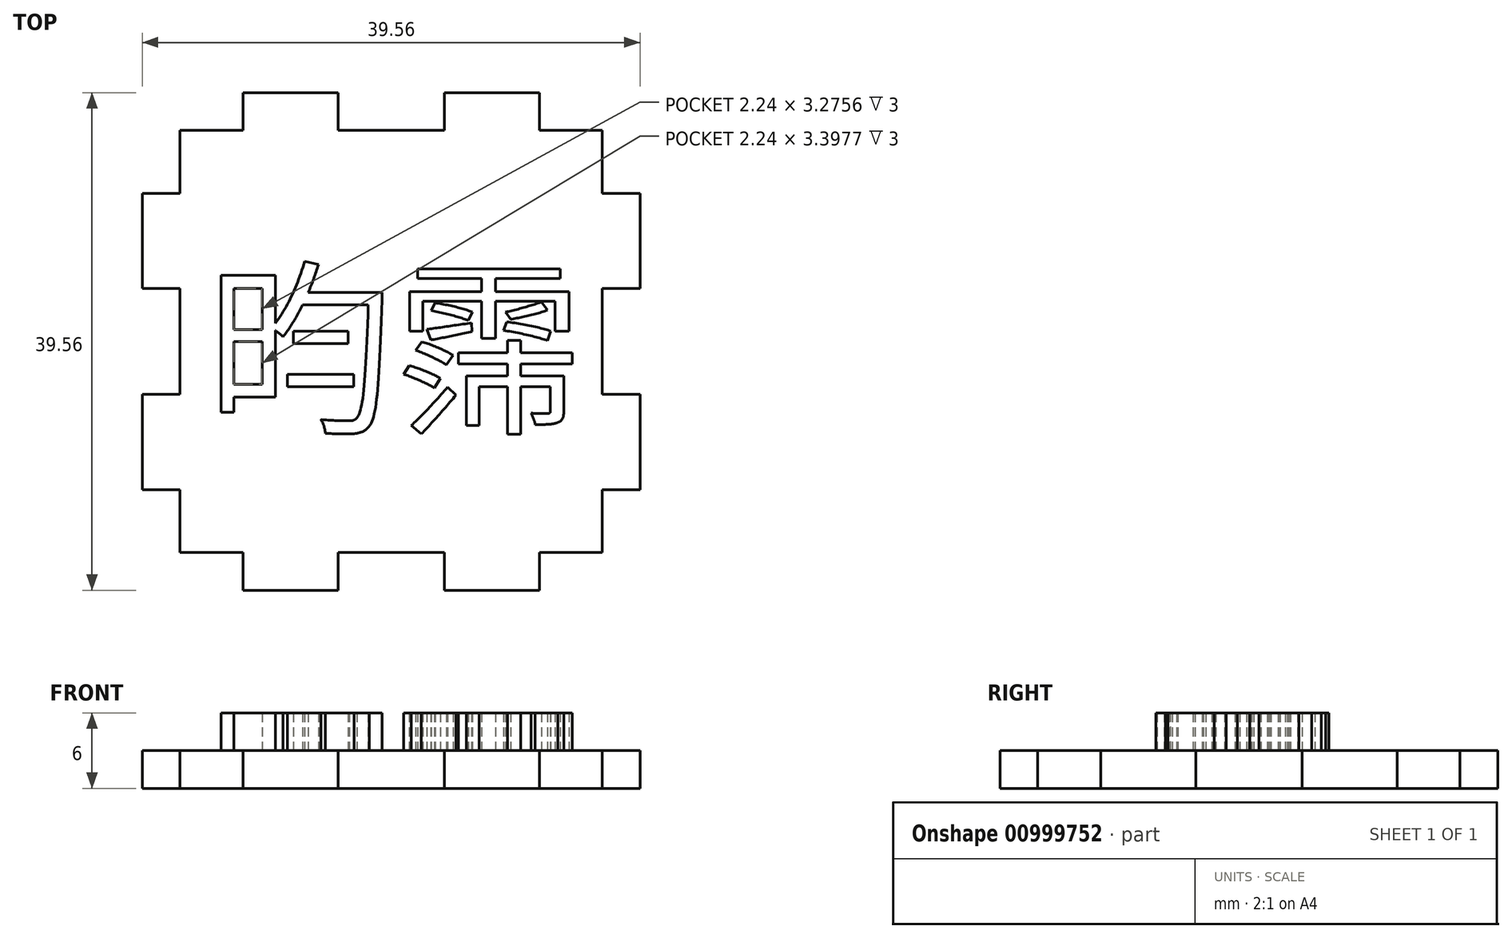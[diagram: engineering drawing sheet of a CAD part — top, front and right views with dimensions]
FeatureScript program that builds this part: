
annotation { "Feature Type Name" : "Feature", "Feature Type Description" : "" }
export const myFeature = defineFeature(function(context is Context, id is Id, definition is map)
    precondition{}
    {
        {
            var Q0;
            Q0=qCreatedBy(makeId("Top.planeOp"),FACE);
            var sketch = newSketch(context, id + "F0", { "sketchPlane" : qUnion([Q0])});
            skLineSegment(sketch, "E0.bottom", {"start": v(17, -17) * mm, "end": v(-17, -17) * mm});
            skLineSegment(sketch, "E0.top", {"start": v(17, 17) * mm, "end": v(-17, 17) * mm});
            skLineSegment(sketch, "E0.left", {"start": v(17, -17) * mm, "end": v(17, 17) * mm});
            skLineSegment(sketch, "E0.right", {"start": v(-17, -17) * mm, "end": v(-17, 17) * mm});
            skPoint(sketch, "E0.middle", {"position": v(0, 0) * mm});
            skSolve(sketch);
        }
        {
            var Q0;
            Q0 = qSketchRegion(id + "F0", true);
            extrude(context, id + "F1", {"entities" : qUnion([Q0]), "depth" : 3 * mm, "offsetDistance" : 25 * mm});
        }
        {
            var Q0;
            Q0=makeQuery(id+"F1.opExtrude","CAP_FACE",FACE,{"disambiguationData":[OSD([sQuery(id+"F0.wireOp",EDGE,"E0.bottom"),sQuery(id+"F0.wireOp",EDGE,"E0.top"),sQuery(id+"F0.wireOp",EDGE,"E0.left"),sQuery(id+"F0.wireOp",EDGE,"E0.right")])],"isStart":false});
            var sketch = newSketch(context, id + "F2", { "sketchPlane" : qUnion([Q0])});
            skLineSegment(sketch, "E1.bottom", {"start": v(-17, 12) * mm, "end": v(-20, 12) * mm});
            skLineSegment(sketch, "E1.top", {"start": v(-17, 4) * mm, "end": v(-20, 4) * mm});
            skLineSegment(sketch, "E1.left", {"start": v(-17, 12) * mm, "end": v(-17, 4) * mm});
            skLineSegment(sketch, "E1.right", {"start": v(-20, 12) * mm, "end": v(-20, 4) * mm});
            skLineSegment(sketch, "E2.MirrorCS", {"start": v(-17, -12) * mm, "end": v(-20, -12) * mm});
            skLineSegment(sketch, "E3.MirrorCS", {"start": v(-17, -12) * mm, "end": v(-17, -4) * mm});
            skLineSegment(sketch, "E4.MirrorCS", {"start": v(-20, -12) * mm, "end": v(-20, -4) * mm});
            skLineSegment(sketch, "E5.MirrorCS", {"start": v(-17, -4) * mm, "end": v(-20, -4) * mm});
            skLineSegment(sketch, "E6.1.0", {"start": v(-4, -17) * mm, "end": v(-4, -20) * mm});
            skLineSegment(sketch, "E6.1.1", {"start": v(4, -17) * mm, "end": v(4, -20) * mm});
            skLineSegment(sketch, "E6.1.2", {"start": v(12, -17) * mm, "end": v(4, -17) * mm});
            skLineSegment(sketch, "E6.1.3", {"start": v(-12, -17) * mm, "end": v(-12, -20) * mm});
            skLineSegment(sketch, "E6.1.4", {"start": v(12, -17) * mm, "end": v(12, -20) * mm});
            skLineSegment(sketch, "E6.1.5", {"start": v(-12, -17) * mm, "end": v(-4, -17) * mm});
            skLineSegment(sketch, "E6.1.6", {"start": v(12, -20) * mm, "end": v(4, -20) * mm});
            skLineSegment(sketch, "E6.1.7", {"start": v(-12, -20) * mm, "end": v(-4, -20) * mm});
            skLineSegment(sketch, "E6.2.0", {"start": v(17, -4) * mm, "end": v(20, -4) * mm});
            skLineSegment(sketch, "E6.2.1", {"start": v(17, 4) * mm, "end": v(20, 4) * mm});
            skLineSegment(sketch, "E6.2.2", {"start": v(17, 12) * mm, "end": v(17, 4) * mm});
            skLineSegment(sketch, "E6.2.3", {"start": v(17, -12) * mm, "end": v(20, -12) * mm});
            skLineSegment(sketch, "E6.2.4", {"start": v(17, 12) * mm, "end": v(20, 12) * mm});
            skLineSegment(sketch, "E6.2.5", {"start": v(17, -12) * mm, "end": v(17, -4) * mm});
            skLineSegment(sketch, "E6.2.6", {"start": v(20, 12) * mm, "end": v(20, 4) * mm});
            skLineSegment(sketch, "E6.2.7", {"start": v(20, -12) * mm, "end": v(20, -4) * mm});
            skLineSegment(sketch, "E6.3.0", {"start": v(4, 17) * mm, "end": v(4, 20) * mm});
            skLineSegment(sketch, "E6.3.1", {"start": v(-4, 17) * mm, "end": v(-4, 20) * mm});
            skLineSegment(sketch, "E6.3.2", {"start": v(-12, 17) * mm, "end": v(-4, 17) * mm});
            skLineSegment(sketch, "E6.3.3", {"start": v(12, 17) * mm, "end": v(12, 20) * mm});
            skLineSegment(sketch, "E6.3.4", {"start": v(-12, 17) * mm, "end": v(-12, 20) * mm});
            skLineSegment(sketch, "E6.3.5", {"start": v(12, 17) * mm, "end": v(4, 17) * mm});
            skLineSegment(sketch, "E6.3.6", {"start": v(-12, 20) * mm, "end": v(-4, 20) * mm});
            skLineSegment(sketch, "E6.3.7", {"start": v(12, 20) * mm, "end": v(4, 20) * mm});
            skPoint(sketch, "E6.center", {"position": v(0, 0) * mm});
            skSolve(sketch);
        }
        {
            var Q0;
            Q0 = qSketchRegion(id + "F2", true);
            extrude(context, id + "F3", {"entities" : qUnion([Q0]), "operationType" : NewBodyOperationType.ADD, "oppositeDirection" : true, "depth" : 3 * mm, "offsetDistance" : 25 * mm});
        }
        {
            var Q0;
            Q0=makeQuery(id+"F3.boolean.opBoolean","MERGE",FACE,{"derivedFrom":[makeQuery(id+"F1.opExtrude","CAP_FACE",FACE,{"disambiguationData":[OSD([sQuery(id+"F0.wireOp",EDGE,"E0.bottom"),sQuery(id+"F0.wireOp",EDGE,"E0.top"),sQuery(id+"F0.wireOp",EDGE,"E0.left"),sQuery(id+"F0.wireOp",EDGE,"E0.right")])],"isStart":false}),makeQuery(id+"F3.opExtrude","CAP_FACE",FACE,{"disambiguationData":[OSD([sQuery(id+"F2.wireOp",EDGE,"E1.bottom"),sQuery(id+"F2.wireOp",EDGE,"E1.top"),sQuery(id+"F2.wireOp",EDGE,"E1.left"),sQuery(id+"F2.wireOp",EDGE,"E1.right")])],"isStart":true}),makeQuery(id+"F3.opExtrude","CAP_FACE",FACE,{"disambiguationData":[OSD([sQuery(id+"F2.wireOp",EDGE,"E2.MirrorCS"),sQuery(id+"F2.wireOp",EDGE,"E3.MirrorCS"),sQuery(id+"F2.wireOp",EDGE,"E4.MirrorCS"),sQuery(id+"F2.wireOp",EDGE,"E5.MirrorCS")])],"isStart":true}),makeQuery(id+"F3.opExtrude","CAP_FACE",FACE,{"disambiguationData":[OSD([sQuery(id+"F2.wireOp",EDGE,"E6.1.0"),sQuery(id+"F2.wireOp",EDGE,"E6.1.3"),sQuery(id+"F2.wireOp",EDGE,"E6.1.5"),sQuery(id+"F2.wireOp",EDGE,"E6.1.7")])],"isStart":true}),makeQuery(id+"F3.opExtrude","CAP_FACE",FACE,{"disambiguationData":[OSD([sQuery(id+"F2.wireOp",EDGE,"E6.1.1"),sQuery(id+"F2.wireOp",EDGE,"E6.1.2"),sQuery(id+"F2.wireOp",EDGE,"E6.1.4"),sQuery(id+"F2.wireOp",EDGE,"E6.1.6")])],"isStart":true}),makeQuery(id+"F3.opExtrude","CAP_FACE",FACE,{"disambiguationData":[OSD([sQuery(id+"F2.wireOp",EDGE,"E6.2.0"),sQuery(id+"F2.wireOp",EDGE,"E6.2.3"),sQuery(id+"F2.wireOp",EDGE,"E6.2.5"),sQuery(id+"F2.wireOp",EDGE,"E6.2.7")])],"isStart":true}),makeQuery(id+"F3.opExtrude","CAP_FACE",FACE,{"disambiguationData":[OSD([sQuery(id+"F2.wireOp",EDGE,"E6.2.1"),sQuery(id+"F2.wireOp",EDGE,"E6.2.2"),sQuery(id+"F2.wireOp",EDGE,"E6.2.4"),sQuery(id+"F2.wireOp",EDGE,"E6.2.6")])],"isStart":true}),makeQuery(id+"F3.opExtrude","CAP_FACE",FACE,{"disambiguationData":[OSD([sQuery(id+"F2.wireOp",EDGE,"E6.3.0"),sQuery(id+"F2.wireOp",EDGE,"E6.3.3"),sQuery(id+"F2.wireOp",EDGE,"E6.3.5"),sQuery(id+"F2.wireOp",EDGE,"E6.3.7")])],"isStart":true}),makeQuery(id+"F3.opExtrude","CAP_FACE",FACE,{"disambiguationData":[OSD([sQuery(id+"F2.wireOp",EDGE,"E6.3.1"),sQuery(id+"F2.wireOp",EDGE,"E6.3.2"),sQuery(id+"F2.wireOp",EDGE,"E6.3.4"),sQuery(id+"F2.wireOp",EDGE,"E6.3.6")])],"isStart":true})]});
            var sketch = newSketch(context, id + "F4", { "sketchPlane" : qUnion([Q0])});
            skLineSegment(sketch, "E7.0", {"start": v(11.78, -16.78) * mm, "end": v(16.78, -16.78) * mm});
            skLineSegment(sketch, "E7.1", {"start": v(11.78, -19.78) * mm, "end": v(11.78, -16.78) * mm});
            skLineSegment(sketch, "E7.2", {"start": v(4.22, -19.78) * mm, "end": v(11.78, -19.78) * mm});
            skLineSegment(sketch, "E7.3", {"start": v(4.22, -16.78) * mm, "end": v(4.22, -19.78) * mm});
            skLineSegment(sketch, "E7.4", {"start": v(-4.22, -16.78) * mm, "end": v(4.22, -16.78) * mm});
            skLineSegment(sketch, "E7.5", {"start": v(-4.22, -19.78) * mm, "end": v(-4.22, -16.78) * mm});
            skLineSegment(sketch, "E7.6", {"start": v(-11.78, -19.78) * mm, "end": v(-4.22, -19.78) * mm});
            skLineSegment(sketch, "E7.7", {"start": v(-11.78, -16.78) * mm, "end": v(-11.78, -19.78) * mm});
            skLineSegment(sketch, "E7.8", {"start": v(-16.78, -16.78) * mm, "end": v(-11.78, -16.78) * mm});
            skLineSegment(sketch, "E7.9", {"start": v(-16.78, -11.78) * mm, "end": v(-16.78, -16.78) * mm});
            skLineSegment(sketch, "E7.10", {"start": v(-19.78, -11.78) * mm, "end": v(-16.78, -11.78) * mm});
            skLineSegment(sketch, "E7.11", {"start": v(16.78, -16.78) * mm, "end": v(16.78, -11.78) * mm});
            skLineSegment(sketch, "E7.12", {"start": v(-19.78, -4.22) * mm, "end": v(-19.78, -11.78) * mm});
            skLineSegment(sketch, "E7.13", {"start": v(-16.78, -4.22) * mm, "end": v(-19.78, -4.22) * mm});
            skLineSegment(sketch, "E7.14", {"start": v(11.78, 16.78) * mm, "end": v(11.78, 19.78) * mm});
            skLineSegment(sketch, "E7.15", {"start": v(16.78, 16.78) * mm, "end": v(11.78, 16.78) * mm});
            skLineSegment(sketch, "E7.16", {"start": v(16.78, 11.78) * mm, "end": v(16.78, 16.78) * mm});
            skLineSegment(sketch, "E7.17", {"start": v(19.78, 11.78) * mm, "end": v(16.78, 11.78) * mm});
            skLineSegment(sketch, "E7.18", {"start": v(19.78, 4.22) * mm, "end": v(19.78, 11.78) * mm});
            skLineSegment(sketch, "E7.19", {"start": v(16.78, 4.22) * mm, "end": v(19.78, 4.22) * mm});
            skLineSegment(sketch, "E7.20", {"start": v(16.78, -11.78) * mm, "end": v(19.78, -11.78) * mm});
            skLineSegment(sketch, "E7.21", {"start": v(19.78, -11.78) * mm, "end": v(19.78, -4.22) * mm});
            skLineSegment(sketch, "E7.22", {"start": v(19.78, -4.22) * mm, "end": v(16.78, -4.22) * mm});
            skLineSegment(sketch, "E7.23", {"start": v(16.78, -4.22) * mm, "end": v(16.78, 4.22) * mm});
            skLineSegment(sketch, "E7.24", {"start": v(11.78, 19.78) * mm, "end": v(4.22, 19.78) * mm});
            skLineSegment(sketch, "E7.25", {"start": v(4.22, 19.78) * mm, "end": v(4.22, 16.78) * mm});
            skLineSegment(sketch, "E7.26", {"start": v(4.22, 16.78) * mm, "end": v(-4.22, 16.78) * mm});
            skLineSegment(sketch, "E7.27", {"start": v(-4.22, 16.78) * mm, "end": v(-4.22, 19.78) * mm});
            skLineSegment(sketch, "E7.28", {"start": v(-4.22, 19.78) * mm, "end": v(-11.78, 19.78) * mm});
            skLineSegment(sketch, "E7.29", {"start": v(-11.78, 19.78) * mm, "end": v(-11.78, 16.78) * mm});
            skLineSegment(sketch, "E7.30", {"start": v(-11.78, 16.78) * mm, "end": v(-16.78, 16.78) * mm});
            skLineSegment(sketch, "E7.31", {"start": v(-16.78, 16.78) * mm, "end": v(-16.78, 11.78) * mm});
            skLineSegment(sketch, "E7.32", {"start": v(-16.78, 11.78) * mm, "end": v(-19.78, 11.78) * mm});
            skLineSegment(sketch, "E7.33", {"start": v(-19.78, 11.78) * mm, "end": v(-19.78, 4.22) * mm});
            skLineSegment(sketch, "E7.34", {"start": v(-19.78, 4.22) * mm, "end": v(-16.78, 4.22) * mm});
            skLineSegment(sketch, "E7.35", {"start": v(-16.78, 4.22) * mm, "end": v(-16.78, -4.22) * mm});
            skLineSegment(sketch, "E8.bottom", {"start": v(25.94, -26.08) * mm, "end": v(-25.94, -26.08) * mm});
            skLineSegment(sketch, "E8.top", {"start": v(25.94, 26.08) * mm, "end": v(-25.94, 26.08) * mm});
            skLineSegment(sketch, "E8.left", {"start": v(25.94, -26.08) * mm, "end": v(25.94, 26.08) * mm});
            skLineSegment(sketch, "E8.right", {"start": v(-25.94, -26.08) * mm, "end": v(-25.94, 26.08) * mm});
            skPoint(sketch, "E8.middle", {"position": v(0, 0) * mm});
            skSolve(sketch);
        }
        {
            var Q0;
            Q0 = qSketchRegion(id + "F4", true);
            extrude(context, id + "F5", {"entities" : qUnion([Q0]), "operationType" : NewBodyOperationType.REMOVE, "endBound" : BoundingType.THROUGH_ALL, "oppositeDirection" : true, "depth" : 25 * mm, "offsetDistance" : 25 * mm});
        }
        {
            var Q0;
            Q0=makeQuery(id+"F3.boolean.opBoolean","MERGE",FACE,{"derivedFrom":[makeQuery(id+"F1.opExtrude","CAP_FACE",FACE,{"disambiguationData":[OSD([sQuery(id+"F0.wireOp",EDGE,"E0.bottom"),sQuery(id+"F0.wireOp",EDGE,"E0.top"),sQuery(id+"F0.wireOp",EDGE,"E0.left"),sQuery(id+"F0.wireOp",EDGE,"E0.right")])],"isStart":false}),makeQuery(id+"F3.opExtrude","CAP_FACE",FACE,{"disambiguationData":[OSD([sQuery(id+"F2.wireOp",EDGE,"E1.bottom"),sQuery(id+"F2.wireOp",EDGE,"E1.top"),sQuery(id+"F2.wireOp",EDGE,"E1.left"),sQuery(id+"F2.wireOp",EDGE,"E1.right")])],"isStart":true}),makeQuery(id+"F3.opExtrude","CAP_FACE",FACE,{"disambiguationData":[OSD([sQuery(id+"F2.wireOp",EDGE,"E2.MirrorCS"),sQuery(id+"F2.wireOp",EDGE,"E3.MirrorCS"),sQuery(id+"F2.wireOp",EDGE,"E4.MirrorCS"),sQuery(id+"F2.wireOp",EDGE,"E5.MirrorCS")])],"isStart":true}),makeQuery(id+"F3.opExtrude","CAP_FACE",FACE,{"disambiguationData":[OSD([sQuery(id+"F2.wireOp",EDGE,"E6.1.0"),sQuery(id+"F2.wireOp",EDGE,"E6.1.3"),sQuery(id+"F2.wireOp",EDGE,"E6.1.5"),sQuery(id+"F2.wireOp",EDGE,"E6.1.7")])],"isStart":true}),makeQuery(id+"F3.opExtrude","CAP_FACE",FACE,{"disambiguationData":[OSD([sQuery(id+"F2.wireOp",EDGE,"E6.1.1"),sQuery(id+"F2.wireOp",EDGE,"E6.1.2"),sQuery(id+"F2.wireOp",EDGE,"E6.1.4"),sQuery(id+"F2.wireOp",EDGE,"E6.1.6")])],"isStart":true}),makeQuery(id+"F3.opExtrude","CAP_FACE",FACE,{"disambiguationData":[OSD([sQuery(id+"F2.wireOp",EDGE,"E6.2.0"),sQuery(id+"F2.wireOp",EDGE,"E6.2.3"),sQuery(id+"F2.wireOp",EDGE,"E6.2.5"),sQuery(id+"F2.wireOp",EDGE,"E6.2.7")])],"isStart":true}),makeQuery(id+"F3.opExtrude","CAP_FACE",FACE,{"disambiguationData":[OSD([sQuery(id+"F2.wireOp",EDGE,"E6.2.1"),sQuery(id+"F2.wireOp",EDGE,"E6.2.2"),sQuery(id+"F2.wireOp",EDGE,"E6.2.4"),sQuery(id+"F2.wireOp",EDGE,"E6.2.6")])],"isStart":true}),makeQuery(id+"F3.opExtrude","CAP_FACE",FACE,{"disambiguationData":[OSD([sQuery(id+"F2.wireOp",EDGE,"E6.3.0"),sQuery(id+"F2.wireOp",EDGE,"E6.3.3"),sQuery(id+"F2.wireOp",EDGE,"E6.3.5"),sQuery(id+"F2.wireOp",EDGE,"E6.3.7")])],"isStart":true}),makeQuery(id+"F3.opExtrude","CAP_FACE",FACE,{"disambiguationData":[OSD([sQuery(id+"F2.wireOp",EDGE,"E6.3.1"),sQuery(id+"F2.wireOp",EDGE,"E6.3.2"),sQuery(id+"F2.wireOp",EDGE,"E6.3.4"),sQuery(id+"F2.wireOp",EDGE,"E6.3.6")])],"isStart":true})]});
            var sketch = newSketch(context, id + "F6", { "sketchPlane" : qUnion([Q0])});
            skText(sketch, "E9", { "text": "昀霈", "fontName": "NotoSansCJKtc-Regular.otf"});
            const initialGuessF6  = {"E9": [-0.01476, -0.00622, 1, 0, 0.01082]};
            skSetInitialGuess(sketch, initialGuessF6);
            skSolve(sketch);
        }
        {
            var Q0;
            Q0 = qSketchRegion(id + "F6", true);
            extrude(context, id + "F7", {"entities" : qUnion([Q0]), "operationType" : NewBodyOperationType.ADD, "depth" : 3 * mm, "offsetDistance" : 25 * mm});
        }
    });
